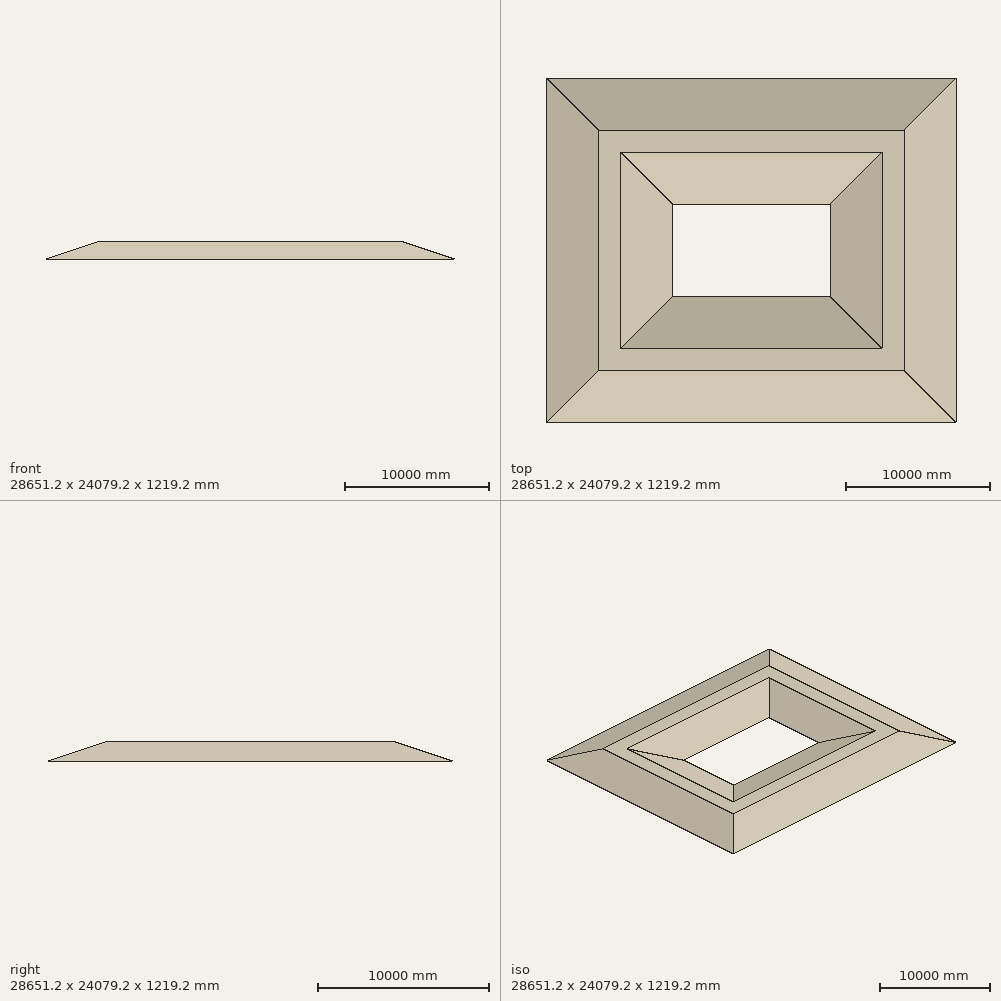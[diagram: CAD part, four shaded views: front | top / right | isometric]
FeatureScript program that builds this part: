
annotation { "Feature Type Name" : "Feature", "Feature Type Description" : "" }
export const myFeature = defineFeature(function(context is Context, id is Id, definition is map)
    precondition{}
    {
        {
            var Q0;
            Q0=qCreatedBy(makeId("Top.planeOp"),FACE);
            var sketch = newSketch(context, id + "F0", { "sketchPlane" : qUnion([Q0])});
            skLineSegment(sketch, "E0.bottom", {"start": v(9144, -6858) * mm, "end": v(-9144, -6858) * mm});
            skLineSegment(sketch, "E0.top", {"start": v(9144, 6858) * mm, "end": v(-9144, 6858) * mm});
            skLineSegment(sketch, "E0.left", {"start": v(9144, -6858) * mm, "end": v(9144, 6858) * mm});
            skLineSegment(sketch, "E0.right", {"start": v(-9144, -6858) * mm, "end": v(-9144, 6858) * mm});
            skPoint(sketch, "E0.middle", {"position": v(0, 0) * mm});
            skLineSegment(sketch, "E1.0", {"start": v(-5486.4, -3200.4) * mm, "end": v(-5486.4, 3200.4) * mm});
            skLineSegment(sketch, "E1.1", {"start": v(5486.4, -3200.4) * mm, "end": v(-5486.4, -3200.4) * mm});
            skLineSegment(sketch, "E1.2", {"start": v(5486.4, -3200.4) * mm, "end": v(5486.4, 3200.4) * mm});
            skLineSegment(sketch, "E1.3", {"start": v(5486.4, 3200.4) * mm, "end": v(-5486.4, 3200.4) * mm});
            skSolve(sketch);
        }
        {
            var Q0;
            Q0=makeQuery(id+"F0.imprint","IMPRINT",FACE,{"disambiguationData":[TD([[makeQuery(id+"F0.imprint","IMPRINT",EDGE,{"derivedFrom":sQuery(id+"F0.wireOp",EDGE,"E0.bottom")}),-1.0]])]});
            cPlane(context, id + "F1", {"entities" : qUnion([Q0]), "cplaneType" : CPlaneType.OFFSET, "offset" : 1219.2 * mm, "width" : 152.4 * mm, "height" : 152.4 * mm});
        }
        {
            var Q0;
            Q0=qCreatedBy(id+"F1.planeOp",FACE);
            var sketch = newSketch(context, id + "F2", { "sketchPlane" : qUnion([Q0])});
            skLineSegment(sketch, "E2.0", {"start": v(9144, 6858) * mm, "end": v(-9144, 6858) * mm});
            skLineSegment(sketch, "E3.0.0", {"start": v(9144, -6858) * mm, "end": v(9144, 6858) * mm});
            skLineSegment(sketch, "E3.0.2", {"start": v(-9144, 6858) * mm, "end": v(-9144, -6858) * mm});
            skLineSegment(sketch, "E3.0.3", {"start": v(-9144, -6858) * mm, "end": v(9144, -6858) * mm});
            skSolve(sketch);
        }
        {
            var Q0;
            Q0=qCreatedBy(makeId("Right.planeOp"),FACE);
            var sketch = newSketch(context, id + "F3", { "sketchPlane" : qUnion([Q0])});
            skPoint(sketch, "E4.0", {"position": v(-6858, 1219.2) * mm});
            skPoint(sketch, "E5.0", {"position": v(-6858, 0) * mm});
            skPoint(sketch, "E6.0", {"position": v(-3200.4, 0) * mm});
            skLineSegment(sketch, "E7", {"start": v(-6858, 1219.2) * mm, "end": v(-6858, 0) * mm});
            skLineSegment(sketch, "E8", {"start": v(-3200.4, 0) * mm, "end": v(-6858, 1219.2) * mm});
            skLineSegment(sketch, "E9", {"start": v(-6858, 0) * mm, "end": v(-3200.4, 0) * mm});
            skLineSegment(sketch, "E10.bottom", {"start": v(-6858, 1219.2) * mm, "end": v(-8382, 1219.2) * mm});
            skLineSegment(sketch, "E10.top", {"start": v(-6858, 0) * mm, "end": v(-8382, 0) * mm});
            skLineSegment(sketch, "E10.right", {"start": v(-8382, 1219.2) * mm, "end": v(-8382, 0) * mm});
            skLineSegment(sketch, "E11", {"start": v(-7620, 1219.2) * mm, "end": v(-7620, 0) * mm, "construction": true});
            skLineSegment(sketch, "E12.MirrorCS", {"start": v(-12039.6, 0) * mm, "end": v(-8382, 1219.2) * mm});
            skLineSegment(sketch, "E13.MirrorCS", {"start": v(-8382, 0) * mm, "end": v(-12039.6, 0) * mm});
            skSolve(sketch);
        }
        {
            var Q0;
            Q0=makeQuery(id+"F3.imprint","IMPRINT",FACE,{"disambiguationData":[TD([[makeQuery(id+"F3.imprint","IMPRINT",EDGE,{"derivedFrom":sQuery(id+"F3.wireOp",EDGE,"E8")}),1.0]])]});
            var Q1;
            Q1=sQuery(id+"F2.wireOp",EDGE,"E3.0.3");
            var Q2;
            Q2=sQuery(id+"F2.wireOp",EDGE,"E3.0.2");
            var Q3;
            Q3=sQuery(id+"F2.wireOp",EDGE,"E2.0");
            var Q4;
            Q4=sQuery(id+"F2.wireOp",EDGE,"E3.0.0");
            sweep(context, id + "F4", {"profiles" : qUnion([Q0]), "path" : qUnion([Q1, Q2, Q3, Q4])});
        }
        {
            var Q0;
            Q0=makeQuery(id+"F3.imprint","IMPRINT",FACE,{"disambiguationData":[TD([[makeQuery(id+"F3.imprint","IMPRINT",EDGE,{"derivedFrom":sQuery(id+"F3.wireOp",EDGE,"E10.bottom")}),1.0]])]});
            var Q1;
            Q1=makeQuery(id+"F4.opSweep","SWEPT_EDGE",EDGE,{"disambiguationData":[OSD([sQuery(id+"F2.wireOp",EDGE,"E3.0.3"),sQuery(id+"F3.wireOp",EDGE,"E8"),sQuery(id+"F3.wireOp",EDGE,"E10.bottom"),sQuery(id+"F3.wireOp",EDGE,"E7")])]});
            var Q2;
            Q2=makeQuery(id+"F4.opSweep","SWEPT_EDGE",EDGE,{"disambiguationData":[OSD([sQuery(id+"F2.wireOp",EDGE,"E3.0.0"),sQuery(id+"F3.wireOp",EDGE,"E8"),sQuery(id+"F3.wireOp",EDGE,"E10.bottom"),sQuery(id+"F3.wireOp",EDGE,"E7")])]});
            var Q3;
            Q3=makeQuery(id+"F4.opSweep","SWEPT_EDGE",EDGE,{"disambiguationData":[OSD([sQuery(id+"F2.wireOp",EDGE,"E2.0"),sQuery(id+"F3.wireOp",EDGE,"E8"),sQuery(id+"F3.wireOp",EDGE,"E10.bottom"),sQuery(id+"F3.wireOp",EDGE,"E7")])]});
            var Q4;
            Q4=makeQuery(id+"F4.opSweep","SWEPT_EDGE",EDGE,{"disambiguationData":[OSD([sQuery(id+"F2.wireOp",EDGE,"E3.0.2"),sQuery(id+"F3.wireOp",EDGE,"E8"),sQuery(id+"F3.wireOp",EDGE,"E10.bottom"),sQuery(id+"F3.wireOp",EDGE,"E7")])]});
            sweep(context, id + "F5", {"profiles" : qUnion([Q0]), "path" : qUnion([Q1, Q2, Q3, Q4])});
        }
        {
            var Q0;
            Q0=makeQuery(id+"F3.imprint","IMPRINT",FACE,{"disambiguationData":[TD([[makeQuery(id+"F3.imprint","IMPRINT",EDGE,{"derivedFrom":sQuery(id+"F3.wireOp",EDGE,"E10.right")}),-1.0]])]});
            var Q1;
            Q1=makeQuery(id+"F5.opSweep","SWEPT_EDGE",EDGE,{"disambiguationData":[OSD([sQuery(id+"F2.wireOp",EDGE,"E3.0.3"),sQuery(id+"F3.wireOp",EDGE,"E8"),sQuery(id+"F3.wireOp",EDGE,"E10.bottom"),sQuery(id+"F3.wireOp",EDGE,"E7"),sQuery(id+"F3.wireOp",EDGE,"E10.right"),sQuery(id+"F3.wireOp",EDGE,"E12.MirrorCS")])]});
            var Q2;
            Q2=makeQuery(id+"F5.opSweep","SWEPT_EDGE",EDGE,{"disambiguationData":[OSD([sQuery(id+"F2.wireOp",EDGE,"E3.0.0"),sQuery(id+"F3.wireOp",EDGE,"E8"),sQuery(id+"F3.wireOp",EDGE,"E10.bottom"),sQuery(id+"F3.wireOp",EDGE,"E7"),sQuery(id+"F3.wireOp",EDGE,"E10.right"),sQuery(id+"F3.wireOp",EDGE,"E12.MirrorCS")])]});
            var Q3;
            Q3=makeQuery(id+"F5.opSweep","SWEPT_EDGE",EDGE,{"disambiguationData":[OSD([sQuery(id+"F2.wireOp",EDGE,"E2.0"),sQuery(id+"F3.wireOp",EDGE,"E8"),sQuery(id+"F3.wireOp",EDGE,"E10.bottom"),sQuery(id+"F3.wireOp",EDGE,"E7"),sQuery(id+"F3.wireOp",EDGE,"E10.right"),sQuery(id+"F3.wireOp",EDGE,"E12.MirrorCS")])]});
            var Q4;
            Q4=makeQuery(id+"F5.opSweep","SWEPT_EDGE",EDGE,{"disambiguationData":[OSD([sQuery(id+"F2.wireOp",EDGE,"E3.0.2"),sQuery(id+"F3.wireOp",EDGE,"E8"),sQuery(id+"F3.wireOp",EDGE,"E10.bottom"),sQuery(id+"F3.wireOp",EDGE,"E7"),sQuery(id+"F3.wireOp",EDGE,"E10.right"),sQuery(id+"F3.wireOp",EDGE,"E12.MirrorCS")])]});
            sweep(context, id + "F6", {"profiles" : qUnion([Q0]), "path" : qUnion([Q1, Q2, Q3, Q4])});
        }
    });
